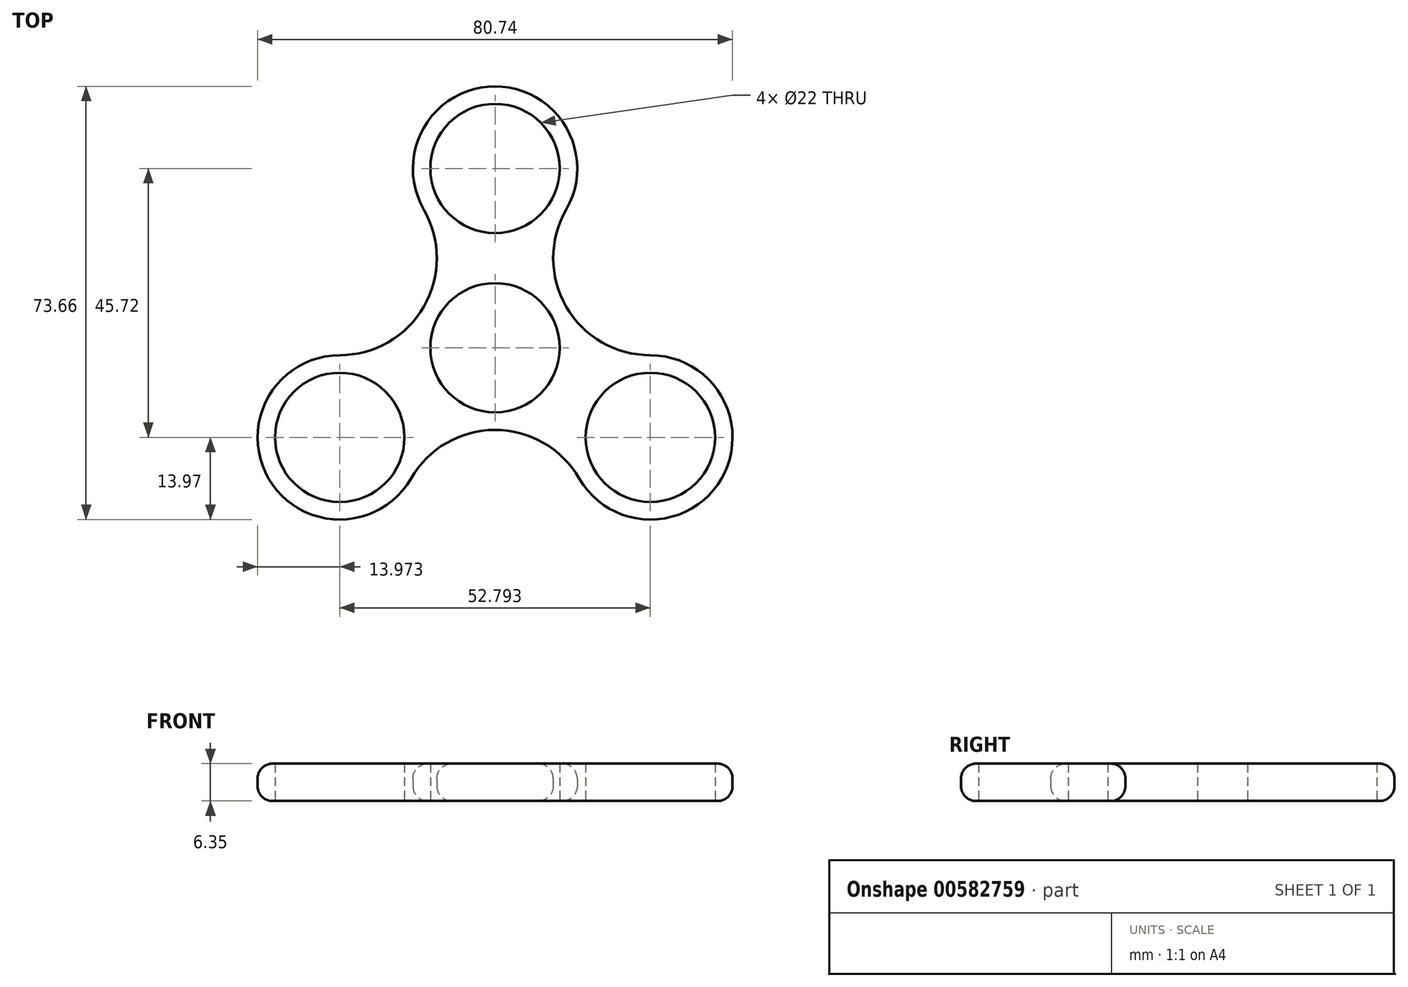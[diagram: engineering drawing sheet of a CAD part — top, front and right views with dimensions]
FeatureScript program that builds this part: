
annotation { "Feature Type Name" : "Feature", "Feature Type Description" : "" }
export const myFeature = defineFeature(function(context is Context, id is Id, definition is map)
    precondition{}
    {
        {
            var Q0;
            Q0=qCreatedBy(makeId("Top.planeOp"),FACE);
            var sketch = newSketch(context, id + "F0", { "sketchPlane" : qUnion([Q0])});
            skCircle(sketch, "E0", {"center": v(0, 0) * mm, "radius": 11 * mm});
            skLineSegment(sketch, "E1", {"start": v(0, 0) * mm, "end": v(0, 30.48) * mm});
            skCircle(sketch, "E2", {"center": v(0, 30.48) * mm, "radius": 11 * mm});
            skCircle(sketch, "E3.1.0", {"center": v(-26.4, -15.24) * mm, "radius": 11 * mm});
            skCircle(sketch, "E3.2.0", {"center": v(26.4, -15.24) * mm, "radius": 11 * mm});
            skCircle(sketch, "E4", {"center": v(-26.4, -15.24) * mm, "radius": 13.97 * mm});
            skCircle(sketch, "E5", {"center": v(26.4, -15.24) * mm, "radius": 13.97 * mm});
            skCircle(sketch, "E6", {"center": v(0, 30.48) * mm, "radius": 13.97 * mm});
            skCircle(sketch, "E7", {"center": v(0, 0) * mm, "radius": 13.97 * mm});
            skLineSegment(sketch, "E8", {"start": v(0, 0) * mm, "end": v(26.4, -15.24) * mm});
            skLineSegment(sketch, "E9", {"start": v(0, 0) * mm, "end": v(49.95, 28.84) * mm});
            skArc(sketch, "E10", {"start": v(12.1, 6.99) * mm, "mid": v(9.89, 15.24) * mm, "end": v(12.1, 23.5) * mm});
            skArc(sketch, "E11", {"start": v(12.1, 6.99) * mm, "mid": v(18.14, 0.94) * mm, "end": v(26.4, -1.27) * mm});
            skArc(sketch, "E12.1.0", {"start": v(-12.1, 6.98) * mm, "mid": v(-18.14, 0.94) * mm, "end": v(-26.4, -1.27) * mm});
            skArc(sketch, "E12.1.1", {"start": v(-12.1, 6.98) * mm, "mid": v(-9.89, 15.24) * mm, "end": v(-12.1, 23.5) * mm});
            skArc(sketch, "E12.2.0", {"start": v(0, -13.97) * mm, "mid": v(8.26, -16.18) * mm, "end": v(14.3, -22.23) * mm});
            skArc(sketch, "E12.2.1", {"start": v(0, -13.97) * mm, "mid": v(-8.25, -16.18) * mm, "end": v(-14.3, -22.22) * mm});
            skSolve(sketch);
        }
        {
            var Q0;
            Q0 = qSketchRegion(id + "F0", true);
            extrude(context, id + "F1", {"entities" : qUnion([Q0]), "depth" : 6.35 * mm, "offsetDistance" : 25.4 * mm});
        }
        {
            var Q0;
            Q0=makeQuery(id+"F1.opExtrude","CAP_EDGE",EDGE,{"disambiguationData":[OSD([sQuery(id+"F0.wireOp",EDGE,"E4")])],"isStart":false});
            var Q1;
            Q1=makeQuery(id+"F1.opExtrude","CAP_EDGE",EDGE,{"disambiguationData":[OSD([sQuery(id+"F0.wireOp",EDGE,"E12.2.0"),sQuery(id+"F0.wireOp",EDGE,"E12.2.1")])],"isStart":false});
            var Q2;
            Q2=makeQuery(id+"F1.opExtrude","CAP_EDGE",EDGE,{"disambiguationData":[OSD([sQuery(id+"F0.wireOp",EDGE,"E5")])],"isStart":false});
            var Q3;
            Q3=makeQuery(id+"F1.opExtrude","CAP_EDGE",EDGE,{"disambiguationData":[OSD([sQuery(id+"F0.wireOp",EDGE,"E6")])],"isStart":false});
            var Q4;
            Q4=makeQuery(id+"F1.opExtrude","CAP_EDGE",EDGE,{"disambiguationData":[OSD([sQuery(id+"F0.wireOp",EDGE,"E10"),sQuery(id+"F0.wireOp",EDGE,"E11")])],"isStart":false});
            var Q5;
            Q5=makeQuery(id+"F1.opExtrude","CAP_EDGE",EDGE,{"disambiguationData":[OSD([sQuery(id+"F0.wireOp",EDGE,"E12.1.0"),sQuery(id+"F0.wireOp",EDGE,"E12.1.1")])],"isStart":false});
            fillet(context, id + "F2", {"entities" : qUnion([Q0, Q1, Q2, Q3, Q4, Q5]), "radius" : 2.54 * mm, "tangentPropagation" : true, "allowEdgeOverflow" : false});
        }
        {
            var Q0;
            Q0=makeQuery(id+"F1.opExtrude","CAP_EDGE",EDGE,{"disambiguationData":[OSD([sQuery(id+"F0.wireOp",EDGE,"E5")])],"isStart":true});
            var Q1;
            Q1=makeQuery(id+"F1.opExtrude","CAP_EDGE",EDGE,{"disambiguationData":[OSD([sQuery(id+"F0.wireOp",EDGE,"E10"),sQuery(id+"F0.wireOp",EDGE,"E11")])],"isStart":true});
            var Q2;
            Q2=makeQuery(id+"F1.opExtrude","CAP_EDGE",EDGE,{"disambiguationData":[OSD([sQuery(id+"F0.wireOp",EDGE,"E6")])],"isStart":true});
            var Q3;
            Q3=makeQuery(id+"F1.opExtrude","CAP_EDGE",EDGE,{"disambiguationData":[OSD([sQuery(id+"F0.wireOp",EDGE,"E12.1.0"),sQuery(id+"F0.wireOp",EDGE,"E12.1.1")])],"isStart":true});
            var Q4;
            Q4=makeQuery(id+"F1.opExtrude","CAP_EDGE",EDGE,{"disambiguationData":[OSD([sQuery(id+"F0.wireOp",EDGE,"E4")])],"isStart":true});
            var Q5;
            Q5=makeQuery(id+"F1.opExtrude","CAP_EDGE",EDGE,{"disambiguationData":[OSD([sQuery(id+"F0.wireOp",EDGE,"E12.2.0"),sQuery(id+"F0.wireOp",EDGE,"E12.2.1")])],"isStart":true});
            fillet(context, id + "F3", {"entities" : qUnion([Q0, Q1, Q2, Q3, Q4, Q5]), "radius" : 2.54 * mm, "tangentPropagation" : true, "allowEdgeOverflow" : false});
        }
    });
